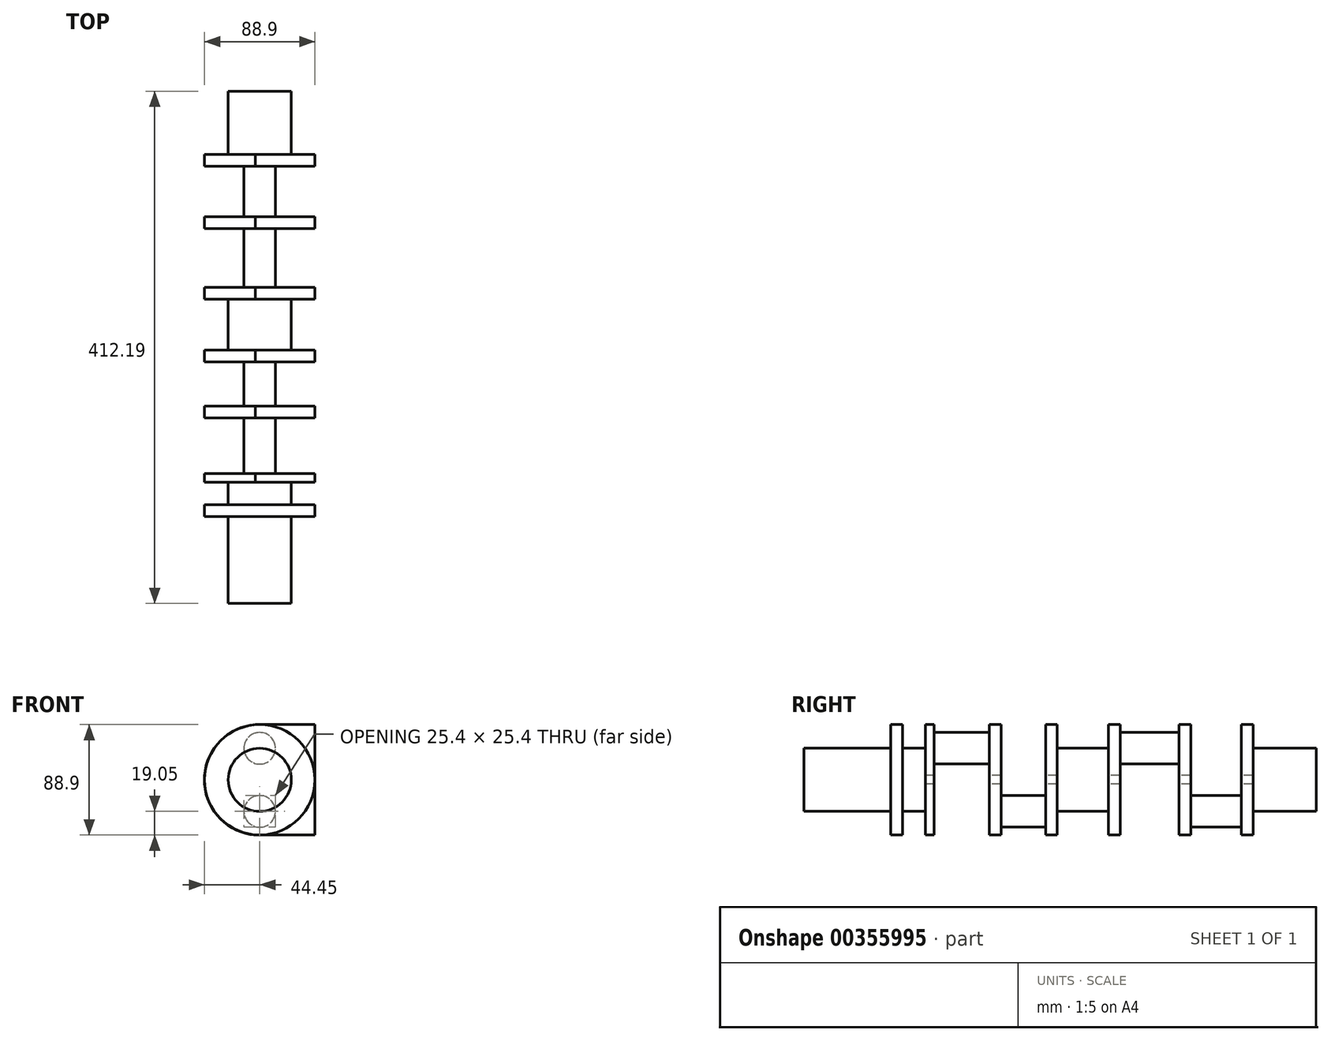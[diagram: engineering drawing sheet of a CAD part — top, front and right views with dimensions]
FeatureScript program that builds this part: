
annotation { "Feature Type Name" : "Feature", "Feature Type Description" : "" }
export const myFeature = defineFeature(function(context is Context, id is Id, definition is map)
    precondition{}
    {
        {
            var Q0;
            Q0=qCreatedBy(makeId("Right.planeOp"),FACE);
            var sketch = newSketch(context, id + "F0", { "sketchPlane" : qUnion([Q0])});
            skLineSegment(sketch, "E0", {"start": v(0, 0) * mm, "end": v(92.38, 0) * mm, "construction": true});
            skLineSegment(sketch, "E1", {"start": v(0, 0) * mm, "end": v(147.88, 0) * mm, "construction": true});
            skLineSegment(sketch, "E2", {"start": v(0, 0) * mm, "end": v(251.13, 0) * mm, "construction": true});
            skLineSegment(sketch, "E3", {"start": v(0, 0) * mm, "end": v(306.63, 0) * mm, "construction": true});
            skLineSegment(sketch, "E4.bottom", {"start": v(50.95, -44.45) * mm, "end": v(41.43, -44.45) * mm});
            skLineSegment(sketch, "E4.top", {"start": v(50.95, 44.45) * mm, "end": v(41.43, 44.45) * mm});
            skLineSegment(sketch, "E4.left", {"start": v(50.95, -44.45) * mm, "end": v(50.95, 44.45) * mm});
            skLineSegment(sketch, "E4.right", {"start": v(41.43, -44.45) * mm, "end": v(41.43, 44.45) * mm});
            skPoint(sketch, "E4.middle", {"position": v(46.19, 0) * mm});
            skLineSegment(sketch, "E5.bottom", {"start": v(69.18, -44.45) * mm, "end": v(78.7, -44.45) * mm});
            skLineSegment(sketch, "E5.top", {"start": v(69.18, 44.45) * mm, "end": v(78.7, 44.45) * mm});
            skLineSegment(sketch, "E5.left", {"start": v(69.18, -44.45) * mm, "end": v(69.18, 44.45) * mm});
            skLineSegment(sketch, "E5.right", {"start": v(78.7, -44.45) * mm, "end": v(78.7, 44.45) * mm});
            skPoint(sketch, "E5.middle", {"position": v(73.94, 0) * mm});
            skLineSegment(sketch, "E6.bottom", {"start": v(120.8, -44.45) * mm, "end": v(130.33, -44.45) * mm});
            skLineSegment(sketch, "E6.top", {"start": v(120.8, 44.45) * mm, "end": v(130.33, 44.45) * mm});
            skLineSegment(sketch, "E6.left", {"start": v(120.8, -44.45) * mm, "end": v(120.8, 44.45) * mm});
            skLineSegment(sketch, "E6.right", {"start": v(130.33, -44.45) * mm, "end": v(130.33, 44.45) * mm});
            skPoint(sketch, "E6.middle", {"position": v(125.56, 0) * mm});
            skLineSegment(sketch, "E7.bottom", {"start": v(165.95, -44.45) * mm, "end": v(175.47, -44.45) * mm});
            skLineSegment(sketch, "E7.top", {"start": v(165.95, 44.45) * mm, "end": v(175.47, 44.45) * mm});
            skLineSegment(sketch, "E7.left", {"start": v(165.95, -44.45) * mm, "end": v(165.95, 44.45) * mm});
            skLineSegment(sketch, "E7.right", {"start": v(175.47, -44.45) * mm, "end": v(175.47, 44.45) * mm});
            skPoint(sketch, "E7.middle", {"position": v(170.71, 0) * mm});
            skLineSegment(sketch, "E8.bottom", {"start": v(282.93, -44.45) * mm, "end": v(273.4, -44.45) * mm});
            skLineSegment(sketch, "E8.top", {"start": v(282.93, 44.45) * mm, "end": v(273.4, 44.45) * mm});
            skLineSegment(sketch, "E8.left", {"start": v(282.93, -44.45) * mm, "end": v(282.93, 44.45) * mm});
            skLineSegment(sketch, "E8.right", {"start": v(273.4, -44.45) * mm, "end": v(273.4, 44.45) * mm});
            skPoint(sketch, "E8.middle", {"position": v(278.17, 0) * mm});
            skLineSegment(sketch, "E9.bottom", {"start": v(226, -44.45) * mm, "end": v(216.47, -44.45) * mm});
            skLineSegment(sketch, "E9.top", {"start": v(226, 44.45) * mm, "end": v(216.47, 44.45) * mm});
            skLineSegment(sketch, "E9.left", {"start": v(226, -44.45) * mm, "end": v(226, 44.45) * mm});
            skLineSegment(sketch, "E9.right", {"start": v(216.47, -44.45) * mm, "end": v(216.47, 44.45) * mm});
            skPoint(sketch, "E9.middle", {"position": v(221.24, 0) * mm});
            skLineSegment(sketch, "E10.bottom", {"start": v(332.97, -44.45) * mm, "end": v(323.44, -44.45) * mm});
            skLineSegment(sketch, "E10.top", {"start": v(332.97, 44.45) * mm, "end": v(323.44, 44.45) * mm});
            skLineSegment(sketch, "E10.left", {"start": v(332.97, -44.45) * mm, "end": v(332.97, 44.45) * mm});
            skLineSegment(sketch, "E10.right", {"start": v(323.44, -44.45) * mm, "end": v(323.44, 44.45) * mm});
            skPoint(sketch, "E10.middle", {"position": v(328.2, 0) * mm});
            skSolve(sketch);
        }
        {
            var Q0;
            Q0=makeQuery(id+"F0.imprint","IMPRINT",FACE,{"disambiguationData":[TD([[makeQuery(id+"F0.imprint","IMPRINT",EDGE,{"derivedFrom":sQuery(id+"F0.wireOp",EDGE,"E4.bottom")}),-1.0]])]});
            var Q1;
            Q1=makeQuery(id+"F0.imprint","IMPRINT",FACE,{"disambiguationData":[TD([[makeQuery(id+"F0.imprint","IMPRINT",EDGE,{"derivedFrom":sQuery(id+"F0.wireOp",EDGE,"E5.bottom")}),1.0]])]});
            var Q2;
            Q2=makeQuery(id+"F0.imprint","IMPRINT",FACE,{"disambiguationData":[TD([[makeQuery(id+"F0.imprint","IMPRINT",EDGE,{"derivedFrom":sQuery(id+"F0.wireOp",EDGE,"E6.bottom")}),1.0]])]});
            var Q3;
            Q3=makeQuery(id+"F0.imprint","IMPRINT",FACE,{"disambiguationData":[TD([[makeQuery(id+"F0.imprint","IMPRINT",EDGE,{"derivedFrom":sQuery(id+"F0.wireOp",EDGE,"E7.bottom")}),1.0]])]});
            var Q4;
            Q4=makeQuery(id+"F0.imprint","IMPRINT",FACE,{"disambiguationData":[TD([[makeQuery(id+"F0.imprint","IMPRINT",EDGE,{"derivedFrom":sQuery(id+"F0.wireOp",EDGE,"E9.bottom")}),-1.0]])]});
            var Q5;
            Q5=makeQuery(id+"F0.imprint","IMPRINT",FACE,{"disambiguationData":[TD([[makeQuery(id+"F0.imprint","IMPRINT",EDGE,{"derivedFrom":sQuery(id+"F0.wireOp",EDGE,"E8.bottom")}),-1.0]])]});
            var Q6;
            Q6=makeQuery(id+"F0.imprint","IMPRINT",FACE,{"disambiguationData":[TD([[makeQuery(id+"F0.imprint","IMPRINT",EDGE,{"derivedFrom":sQuery(id+"F0.wireOp",EDGE,"E10.bottom")}),-1.0]])]});
            extrude(context, id + "F1", {"entities" : qUnion([Q0, Q1, Q2, Q3, Q4, Q5, Q6]), "depth" : 88.9 * mm});
        }
        {
            var Q0;
            Q0=makeQuery(id+"F1.opExtrude","SWEPT_FACE",FACE,{"disambiguationData":[OSD([sQuery(id+"F0.wireOp",EDGE,"E4.right")])]});
            var sketch = newSketch(context, id + "F2", { "sketchPlane" : qUnion([Q0])});
            skCircle(sketch, "E11", {"center": v(44.45, 0) * mm, "radius": 25.4 * mm});
            skPoint(sketch, "E11.centerSnap0", {"position": v(44.45, -44.45) * mm});
            skCircle(sketch, "E12", {"center": v(44.45, 0) * mm, "radius": 44.45 * mm});
            skSolve(sketch);
        }
        {
            var Q0;
            Q0=makeQuery(id+"F2.imprint","IMPRINT",FACE,{"disambiguationData":[TD([[makeQuery(id+"F2.imprint","IMPRINT",EDGE,{"derivedFrom":sQuery(id+"F2.wireOp",EDGE,"E11")}),1.0]])]});
            extrude(context, id + "F3", {"entities" : qUnion([Q0]), "operationType" : NewBodyOperationType.ADD, "depth" : 69.85 * mm, "hasSecondDirection" : true, "secondDirectionOppositeDirection" : true, "secondDirectionDepth" : 30.73 * mm});
        }
        {
            var Q0;
            {var subQ0=sQuery(id+"F2.wireOp",EDGE,"E12");var subQ1=sQuery(id+"F0.wireOp",EDGE,"E4.right");var subQ4=makeQuery(id+"F1.opExtrude","CAP_EDGE",EDGE,{"disambiguationData":[OSD([subQ1])],"isStart":false});var subQ5=makeQuery(id+"F2.imprint","INTERSECT",VERTEX,{"derivedFrom":[subQ4,subQ0]});Q0=makeQuery(id+"F2.imprint","IMPRINT",FACE,{"disambiguationData":[TD([[makeQuery(id+"F2.imprint","IMPRINT",EDGE,{"disambiguationData":[TD([[subQ5,-1.0]])],"derivedFrom":subQ0}),-1.0]])]});}
            var Q1;
            {var subQ0=sQuery(id+"F2.wireOp",EDGE,"E12");var subQ1=sQuery(id+"F0.wireOp",EDGE,"E4.right");var subQ4=makeQuery(id+"F1.opExtrude","CAP_EDGE",EDGE,{"disambiguationData":[OSD([subQ1])],"isStart":true});var subQ5=makeQuery(id+"F2.imprint","INTERSECT",VERTEX,{"derivedFrom":[subQ4,subQ0]});Q1=makeQuery(id+"F2.imprint","IMPRINT",FACE,{"disambiguationData":[TD([[makeQuery(id+"F2.imprint","IMPRINT",EDGE,{"disambiguationData":[TD([[subQ5,1.0]])],"derivedFrom":subQ0}),-1.0]])]});}
            var Q2;
            {var subQ0=sQuery(id+"F2.wireOp",EDGE,"E12");var subQ1=sQuery(id+"F0.wireOp",EDGE,"E4.right");var subQ2=makeQuery(id+"F1.opExtrude","CAP_EDGE",EDGE,{"disambiguationData":[OSD([subQ1])],"isStart":true});var subQ3=makeQuery(id+"F2.imprint","INTERSECT",VERTEX,{"derivedFrom":[subQ2,subQ0]});Q2=makeQuery(id+"F2.imprint","IMPRINT",FACE,{"disambiguationData":[TD([[makeQuery(id+"F2.imprint","IMPRINT",EDGE,{"disambiguationData":[TD([[subQ3,-1.0]])],"derivedFrom":subQ0}),-1.0]])]});}
            var Q3;
            {var subQ0=sQuery(id+"F2.wireOp",EDGE,"E12");var subQ1=sQuery(id+"F0.wireOp",EDGE,"E4.right");var subQ2=makeQuery(id+"F1.opExtrude","CAP_EDGE",EDGE,{"disambiguationData":[OSD([subQ1])],"isStart":false});var subQ3=makeQuery(id+"F2.imprint","INTERSECT",VERTEX,{"derivedFrom":[subQ2,subQ0]});Q3=makeQuery(id+"F2.imprint","IMPRINT",FACE,{"disambiguationData":[TD([[makeQuery(id+"F2.imprint","IMPRINT",EDGE,{"disambiguationData":[TD([[subQ3,1.0]])],"derivedFrom":subQ0}),-1.0]])]});}
            var Q4;
            Q4=makeQuery(id+"F1.opExtrude","SWEPT_FACE",FACE,{"disambiguationData":[OSD([sQuery(id+"F0.wireOp",EDGE,"E10.left")])]});
            extrude(context, id + "F4", {"entities" : qUnion([Q0, Q1, Q2, Q3]), "operationType" : NewBodyOperationType.REMOVE, "oppositeDirection" : true, "endBoundEntityFace" : qUnion([Q4]), "depth" : 12.2 * mm});
        }
        {
            var Q0;
            Q0=makeQuery(id+"F1.opExtrude","SWEPT_FACE",FACE,{"disambiguationData":[OSD([sQuery(id+"F0.wireOp",EDGE,"E6.left")])]});
            var sketch = newSketch(context, id + "F5", { "sketchPlane" : qUnion([Q0])});
            skLineSegment(sketch, "E13", {"start": v(44.45, 44.45) * mm, "end": v(44.45, 25.4) * mm, "construction": true});
            skPoint(sketch, "E13.endSnap0", {"position": v(44.45, 44.45) * mm});
            skCircle(sketch, "E14", {"center": v(44.45, 25.4) * mm, "radius": 12.7 * mm});
            skSolve(sketch);
        }
        {
            var Q0;
            Q0=makeQuery(id+"F5.imprint","IMPRINT",FACE,{"disambiguationData":[TD([[makeQuery(id+"F5.imprint","IMPRINT",EDGE,{"derivedFrom":sQuery(id+"F5.wireOp",EDGE,"E14")}),1.0]])]});
            var Q1;
            Q1=makeQuery(id+"F1.opExtrude","SWEPT_FACE",FACE,{"disambiguationData":[OSD([sQuery(id+"F0.wireOp",EDGE,"E5.right")])]});
            extrude(context, id + "F6", {"entities" : qUnion([Q0]), "operationType" : NewBodyOperationType.ADD, "endBound" : BoundingType.UP_TO_SURFACE, "endBoundEntityFace" : qUnion([Q1]), "depth" : 25.4 * mm});
        }
        {
            var Q0;
            Q0=makeQuery(id+"F1.opExtrude","SWEPT_FACE",FACE,{"disambiguationData":[OSD([sQuery(id+"F0.wireOp",EDGE,"E6.right")])]});
            var sketch = newSketch(context, id + "F7", { "sketchPlane" : qUnion([Q0])});
            skLineSegment(sketch, "E15", {"start": v(-44.45, -44.45) * mm, "end": v(-44.45, -25.4) * mm, "construction": true});
            skCircle(sketch, "E16", {"center": v(-44.45, -25.4) * mm, "radius": 12.7 * mm});
            skSolve(sketch);
        }
        {
            var Q0;
            Q0=makeQuery(id+"F7.imprint","IMPRINT",FACE,{"disambiguationData":[TD([[makeQuery(id+"F7.imprint","IMPRINT",EDGE,{"derivedFrom":sQuery(id+"F7.wireOp",EDGE,"E16")}),1.0]])]});
            var Q1;
            Q1=makeQuery(id+"F1.opExtrude","SWEPT_FACE",FACE,{"disambiguationData":[OSD([sQuery(id+"F0.wireOp",EDGE,"E7.left")])]});
            extrude(context, id + "F8", {"entities" : qUnion([Q0]), "operationType" : NewBodyOperationType.ADD, "endBound" : BoundingType.UP_TO_SURFACE, "endBoundEntityFace" : qUnion([Q1]), "depth" : 25.4 * mm});
        }
        {
            var Q0;
            Q0=makeQuery(id+"F1.opExtrude","SWEPT_FACE",FACE,{"disambiguationData":[OSD([sQuery(id+"F0.wireOp",EDGE,"E7.right")])]});
            var sketch = newSketch(context, id + "F9", { "sketchPlane" : qUnion([Q0])});
            skCircle(sketch, "E17", {"center": v(-44.45, 0) * mm, "radius": 25.4 * mm});
            skPoint(sketch, "E17.centerSnap0", {"position": v(-44.45, 44.45) * mm});
            skSolve(sketch);
        }
        {
            var Q0;
            Q0=makeQuery(id+"F9.imprint","IMPRINT",FACE,{"disambiguationData":[TD([[makeQuery(id+"F9.imprint","IMPRINT",EDGE,{"derivedFrom":sQuery(id+"F9.wireOp",EDGE,"E17")}),1.0]])]});
            var Q1;
            Q1=makeQuery(id+"F1.opExtrude","SWEPT_FACE",FACE,{"disambiguationData":[OSD([sQuery(id+"F0.wireOp",EDGE,"E9.right")])]});
            extrude(context, id + "F10", {"entities" : qUnion([Q0]), "operationType" : NewBodyOperationType.ADD, "endBound" : BoundingType.UP_TO_SURFACE, "endBoundEntityFace" : qUnion([Q1]), "depth" : 25.4 * mm});
        }
        {
            var Q0;
            Q0=makeQuery(id+"F1.opExtrude","SWEPT_FACE",FACE,{"disambiguationData":[OSD([sQuery(id+"F0.wireOp",EDGE,"E9.left")])]});
            var sketch = newSketch(context, id + "F11", { "sketchPlane" : qUnion([Q0])});
            skLineSegment(sketch, "E18", {"start": v(-44.45, 44.45) * mm, "end": v(-44.45, 25.4) * mm, "construction": true});
            skPoint(sketch, "E18.endSnap0", {"position": v(-44.45, 44.45) * mm});
            skCircle(sketch, "E19", {"center": v(-44.45, 25.4) * mm, "radius": 12.7 * mm});
            skSolve(sketch);
        }
        {
            var Q0;
            Q0=makeQuery(id+"F11.imprint","IMPRINT",FACE,{"disambiguationData":[TD([[makeQuery(id+"F11.imprint","IMPRINT",EDGE,{"derivedFrom":sQuery(id+"F11.wireOp",EDGE,"E19")}),1.0]])]});
            var Q1;
            Q1=makeQuery(id+"F1.opExtrude","SWEPT_FACE",FACE,{"disambiguationData":[OSD([sQuery(id+"F0.wireOp",EDGE,"E8.right")])]});
            extrude(context, id + "F12", {"entities" : qUnion([Q0]), "operationType" : NewBodyOperationType.ADD, "endBound" : BoundingType.UP_TO_SURFACE, "endBoundEntityFace" : qUnion([Q1]), "depth" : 25.4 * mm});
        }
        {
            var Q0;
            Q0=makeQuery(id+"F1.opExtrude","SWEPT_FACE",FACE,{"disambiguationData":[OSD([sQuery(id+"F0.wireOp",EDGE,"E8.left")])]});
            var sketch = newSketch(context, id + "F13", { "sketchPlane" : qUnion([Q0])});
            skLineSegment(sketch, "E20", {"start": v(-44.45, -44.45) * mm, "end": v(-44.45, -25.4) * mm, "construction": true});
            skCircle(sketch, "E21", {"center": v(-44.45, -25.4) * mm, "radius": 12.7 * mm});
            skSolve(sketch);
        }
        {
            var Q0;
            Q0=qSketchRegion(id+"F13",true);
            var Q1;
            Q1=makeQuery(id+"F1.opExtrude","SWEPT_FACE",FACE,{"disambiguationData":[OSD([sQuery(id+"F0.wireOp",EDGE,"E10.right")])]});
            extrude(context, id + "F14", {"entities" : qUnion([Q0]), "operationType" : NewBodyOperationType.ADD, "endBound" : BoundingType.UP_TO_SURFACE, "endBoundEntityFace" : qUnion([Q1]), "depth" : 25.4 * mm});
        }
        {
            var Q0;
            Q0=makeQuery(id+"F1.opExtrude","SWEPT_FACE",FACE,{"disambiguationData":[OSD([sQuery(id+"F0.wireOp",EDGE,"E5.left")])]});
            var sketch = newSketch(context, id + "F15", { "sketchPlane" : qUnion([Q0])});
            skCircle(sketch, "E22", {"center": v(44.45, 0) * mm, "radius": 44.59 * mm});
            skSolve(sketch);
        }
        {
            var Q0;
            {var subQ0=sQuery(id+"F15.wireOp",EDGE,"E22");var subQ1=sQuery(id+"F0.wireOp",EDGE,"E5.left");var subQ4=makeQuery(id+"F1.opExtrude","CAP_EDGE",EDGE,{"disambiguationData":[OSD([subQ1])],"isStart":true});var subQ5=makeQuery(id+"F15.imprint","INTERSECT",VERTEX,{"disambiguationData":[OD(0.0)],"derivedFrom":[subQ4,subQ0]});Q0=makeQuery(id+"F15.imprint","IMPRINT",FACE,{"disambiguationData":[TD([[makeQuery(id+"F15.imprint","IMPRINT",EDGE,{"disambiguationData":[TD([[subQ5,1.0]])],"derivedFrom":subQ0}),-1.0]])]});}
            var Q1;
            {var subQ0=sQuery(id+"F15.wireOp",EDGE,"E22");var subQ1=sQuery(id+"F0.wireOp",EDGE,"E5.left");var subQ2=makeQuery(id+"F1.opExtrude","CAP_EDGE",EDGE,{"disambiguationData":[OSD([subQ1])],"isStart":true});var subQ3=makeQuery(id+"F15.imprint","INTERSECT",VERTEX,{"disambiguationData":[OD(1.0)],"derivedFrom":[subQ2,subQ0]});Q1=makeQuery(id+"F15.imprint","IMPRINT",FACE,{"disambiguationData":[TD([[makeQuery(id+"F15.imprint","IMPRINT",EDGE,{"disambiguationData":[TD([[subQ3,-1.0]])],"derivedFrom":subQ0}),-1.0]])]});}
            var Q2;
            {var subQ0=sQuery(id+"F15.wireOp",EDGE,"E22");var subQ1=sQuery(id+"F0.wireOp",EDGE,"E5.left");var subQ4=makeQuery(id+"F1.opExtrude","CAP_EDGE",EDGE,{"disambiguationData":[OSD([subQ1])],"isStart":false});var subQ5=makeQuery(id+"F15.imprint","INTERSECT",VERTEX,{"disambiguationData":[OD(1.0)],"derivedFrom":[subQ4,subQ0]});Q2=makeQuery(id+"F15.imprint","IMPRINT",FACE,{"disambiguationData":[TD([[makeQuery(id+"F15.imprint","IMPRINT",EDGE,{"disambiguationData":[TD([[subQ5,1.0]])],"derivedFrom":subQ0}),-1.0]])]});}
            var Q3;
            {var subQ0=sQuery(id+"F15.wireOp",EDGE,"E22");var subQ1=sQuery(id+"F0.wireOp",EDGE,"E5.left");var subQ4=makeQuery(id+"F1.opExtrude","CAP_EDGE",EDGE,{"disambiguationData":[OSD([subQ1])],"isStart":false});var subQ5=makeQuery(id+"F15.imprint","INTERSECT",VERTEX,{"disambiguationData":[OD(0.0)],"derivedFrom":[subQ4,subQ0]});Q3=makeQuery(id+"F15.imprint","IMPRINT",FACE,{"disambiguationData":[TD([[makeQuery(id+"F15.imprint","IMPRINT",EDGE,{"disambiguationData":[TD([[subQ5,-1.0]])],"derivedFrom":subQ0}),-1.0]])]});}
            extrude(context, id + "F16", {"entities" : qUnion([Q0, Q1, Q2, Q3]), "operationType" : NewBodyOperationType.REMOVE, "endBound" : BoundingType.THROUGH_ALL, "oppositeDirection" : true, "depth" : 25.4 * mm});
        }
        {
            var Q0;
            Q0=makeQuery(id+"F1.opExtrude","SWEPT_FACE",FACE,{"disambiguationData":[OSD([sQuery(id+"F0.wireOp",EDGE,"E10.left")])]});
            var sketch = newSketch(context, id + "F17", { "sketchPlane" : qUnion([Q0])});
            skCircle(sketch, "E23", {"center": v(-44.45, 0) * mm, "radius": 25.4 * mm});
            skSolve(sketch);
        }
        {
            var Q0;
            Q0=qSketchRegion(id+"F17",true);
            extrude(context, id + "F18", {"entities" : qUnion([Q0]), "operationType" : NewBodyOperationType.ADD, "depth" : 50.8 * mm});
        }
        {
            var Q0;
            Q0=makeQuery(id+"F1.opExtrude","SWEPT_FACE",FACE,{"disambiguationData":[OSD([sQuery(id+"F0.wireOp",EDGE,"E5.right")])]});
            extrude(context, id + "F19", {"entities" : qUnion([Q0]), "operationType" : NewBodyOperationType.REMOVE, "oppositeDirection" : true, "depth" : 2.54 * mm});
        }
    });
